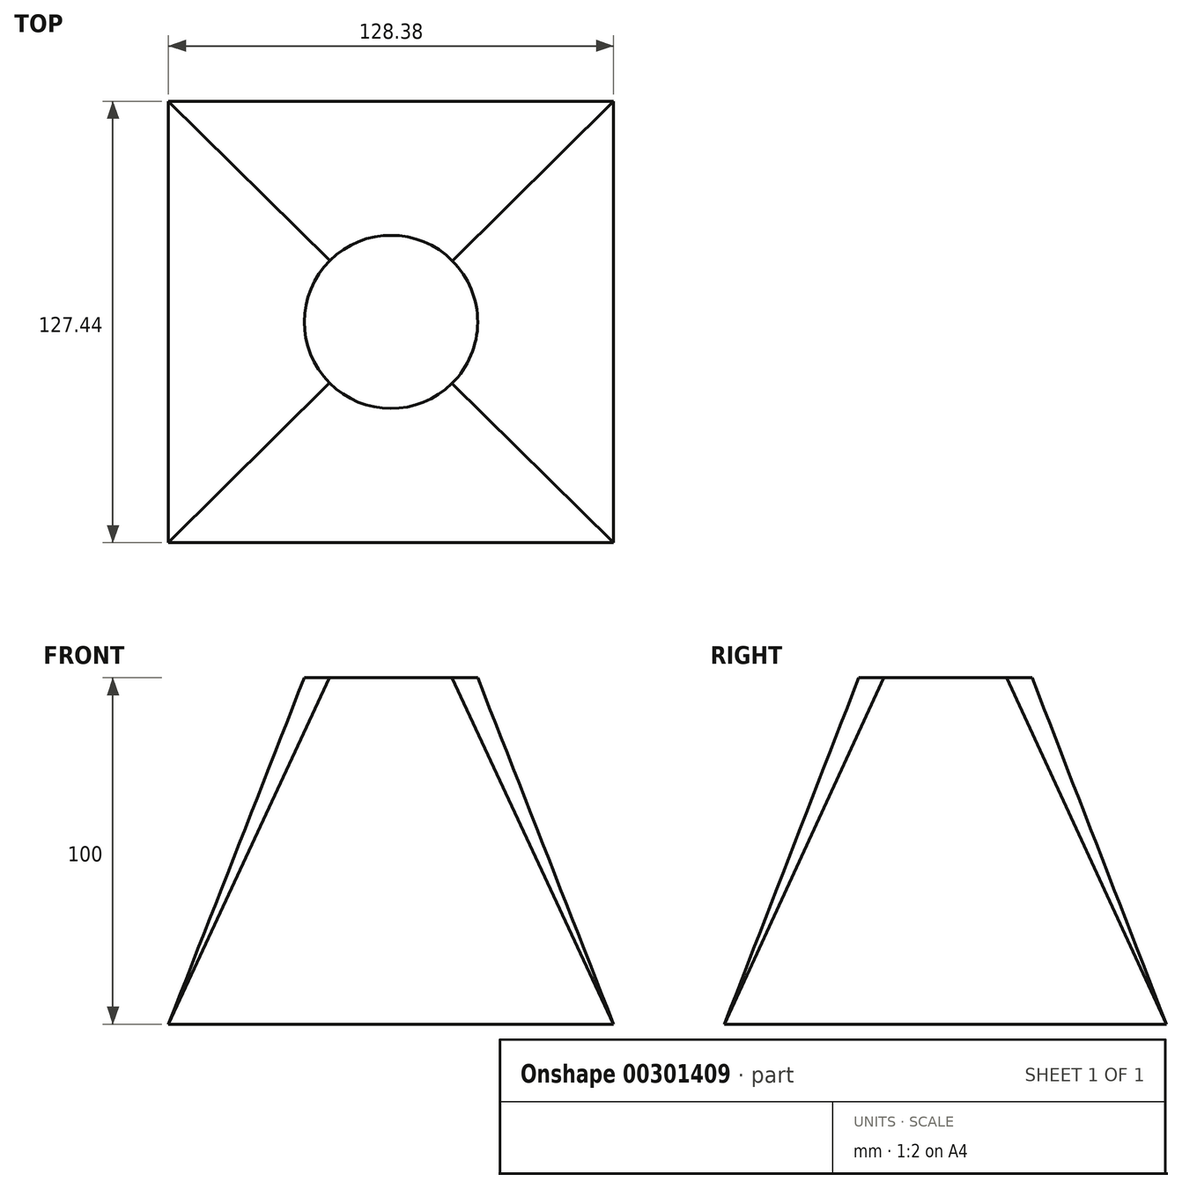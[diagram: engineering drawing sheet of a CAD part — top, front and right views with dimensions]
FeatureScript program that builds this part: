
annotation { "Feature Type Name" : "Feature", "Feature Type Description" : "" }
export const myFeature = defineFeature(function(context is Context, id is Id, definition is map)
    precondition{}
    {
        {
            var Q0;
            Q0=qCreatedBy(makeId("Top.planeOp"),FACE);
            var sketch = newSketch(context, id + "F0", { "sketchPlane" : qUnion([Q0])});
            skLineSegment(sketch, "E0.bottom", {"start": v(64.19, 63.72) * mm, "end": v(-64.19, 63.72) * mm});
            skLineSegment(sketch, "E0.top", {"start": v(64.19, -63.72) * mm, "end": v(-64.19, -63.72) * mm});
            skLineSegment(sketch, "E0.left", {"start": v(64.19, 63.72) * mm, "end": v(64.19, -63.72) * mm});
            skLineSegment(sketch, "E0.right", {"start": v(-64.19, 63.72) * mm, "end": v(-64.19, -63.72) * mm});
            skPoint(sketch, "E0.middle", {"position": v(0, 0) * mm});
            skSolve(sketch);
        }
        {
            var Q0;
            Q0=qCreatedBy(makeId("Top.planeOp"),FACE);
            cPlane(context, id + "F1", {"entities" : qUnion([Q0]), "cplaneType" : CPlaneType.OFFSET, "offset" : 100 * mm, "width" : 150 * mm, "height" : 150 * mm});
        }
        {
            var Q0;
            Q0=qCreatedBy(id+"F1.planeOp",FACE);
            var sketch = newSketch(context, id + "F2", { "sketchPlane" : qUnion([Q0])});
            skCircle(sketch, "E1", {"center": v(0, 0) * mm, "radius": 25 * mm});
            skSolve(sketch);
        }
        {
            var Q0;
            Q0=makeQuery(id+"F0.imprint","IMPRINT",FACE,{"disambiguationData":[TD([[makeQuery(id+"F0.imprint","IMPRINT",EDGE,{"derivedFrom":sQuery(id+"F0.wireOp",EDGE,"E0.bottom")}),1.0]])]});
            var Q1;
            Q1=makeQuery(id+"F2.imprint","IMPRINT",FACE,{"disambiguationData":[TD([[makeQuery(id+"F2.imprint","IMPRINT",EDGE,{"derivedFrom":sQuery(id+"F2.wireOp",EDGE,"E1")}),1.0]])]});
            loft(context, id + "F3", {"sheetProfilesArray" : [{ "sheetProfileEntities" : qUnion([Q0]) }, { "sheetProfileEntities" : qUnion([Q1]) }]});
        }
    });
